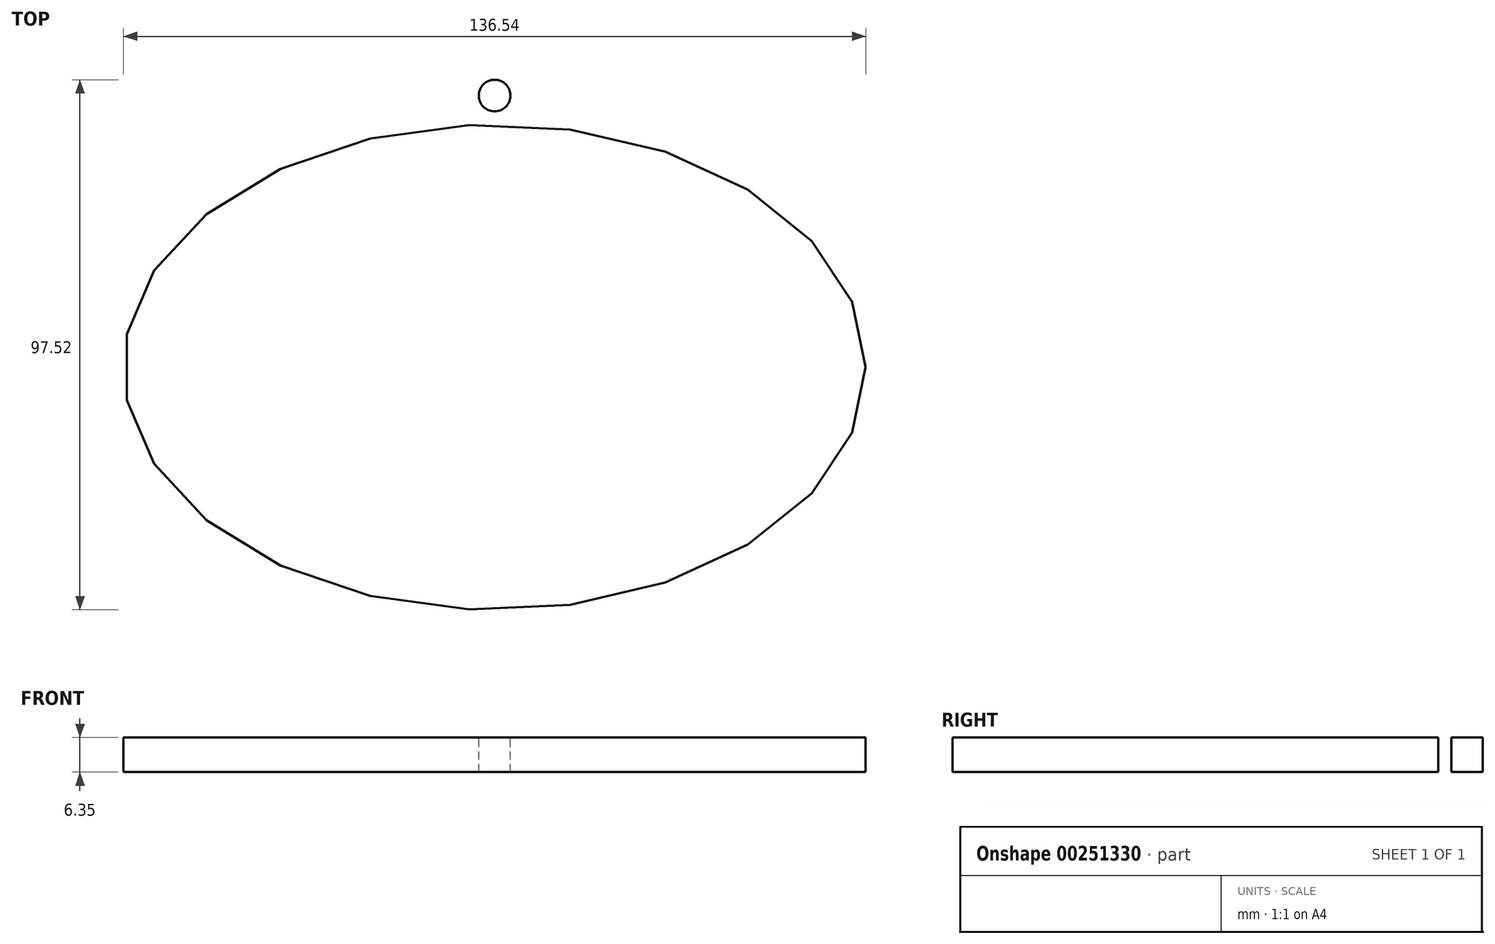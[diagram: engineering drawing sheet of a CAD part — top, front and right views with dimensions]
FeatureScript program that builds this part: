
annotation { "Feature Type Name" : "Feature", "Feature Type Description" : "" }
export const myFeature = defineFeature(function(context is Context, id is Id, definition is map)
    precondition{}
    {
        {
            var Q0;
            Q0=qCreatedBy(makeId("Top.planeOp"),FACE);
            var sketch = newSketch(context, id + "F0", { "sketchPlane" : qUnion([Q0])});
            skEllipse(sketch, "E0", {"center": v(-42.45, 33.5) * mm, "majorRadius": 68.27 * mm, "minorRadius": 44.64 * mm, "majorAxis": v(1, 0)});
            skFitSpline(sketch, "E1.0", {"points": [v(35.9, 30.52) * mm, v(36.01, 33.5) * mm, v(35.9, 36.5) * mm, v(35.45, 40.43) * mm, v(34.34, 45.26) * mm, v(32.2, 50.82) * mm, v(29.32, 56.08) * mm, v(25.75, 61) * mm, v(21.56, 65.59) * mm, v(17.58, 69.1) * mm, v(14.13, 71.72) * mm, v(11.4, 73.6) * mm, v(8.56, 75.36) * mm, v(4.65, 77.56) * mm, v(-0.46, 80.03) * mm, v(-6.91, 82.55) * mm, v(-13.63, 84.63) * mm, v(-20.58, 86.26) * mm, v(-27.73, 87.43) * mm, v(-33.81, 88.03) * mm, v(-38.73, 88.27) * mm, v(-42.45, 88.33) * mm, v(-46.17, 88.27) * mm, v(-51.1, 88.03) * mm, v(-57.18, 87.43) * mm, v(-64.32, 86.26) * mm, v(-71.27, 84.63) * mm, v(-78, 82.55) * mm, v(-84.44, 80.03) * mm, v(-89.55, 77.56) * mm, v(-93.46, 75.36) * mm, v(-96.3, 73.6) * mm, v(-99.03, 71.72) * mm, v(-102.48, 69.1) * mm, v(-106.46, 65.59) * mm, v(-110.65, 61) * mm, v(-114.22, 56.08) * mm, v(-117.1, 50.82) * mm, v(-119.25, 45.26) * mm, v(-120.35, 40.43) * mm, v(-120.8, 36.5) * mm, v(-120.92, 33.5) * mm, v(-120.8, 30.52) * mm, v(-120.35, 26.57) * mm, v(-119.25, 21.74) * mm, v(-117.1, 16.19) * mm, v(-114.22, 10.93) * mm, v(-110.65, 6) * mm, v(-106.46, 1.42) * mm, v(-102.48, -2.1) * mm, v(-99.03, -4.71) * mm, v(-96.3, -6.59) * mm, v(-93.46, -8.35) * mm, v(-89.55, -10.55) * mm, v(-84.44, -13.03) * mm, v(-78, -15.55) * mm, v(-71.27, -17.62) * mm, v(-64.32, -19.25) * mm, v(-57.18, -20.43) * mm, v(-51.1, -21.02) * mm, v(-46.17, -21.26) * mm, v(-42.45, -21.32) * mm, v(-38.73, -21.26) * mm, v(-33.81, -21.02) * mm, v(-27.73, -20.43) * mm, v(-20.58, -19.25) * mm, v(-13.63, -17.62) * mm, v(-6.91, -15.55) * mm, v(-0.46, -13.03) * mm, v(4.65, -10.55) * mm, v(8.56, -8.35) * mm, v(11.4, -6.59) * mm, v(14.13, -4.71) * mm, v(17.58, -2.1) * mm, v(21.56, 1.42) * mm, v(25.75, 6) * mm, v(29.32, 10.93) * mm, v(32.2, 16.19) * mm, v(34.34, 21.74) * mm, v(35.45, 26.57) * mm, v(35.9, 30.52) * mm, v(36.01, 33.5) * mm, v(35.9, 36.5) * mm, v(35.9, 30.52) * mm]});
            skCircle(sketch, "E2", {"center": v(-42.45, 83.47) * mm, "radius": 2.9 * mm});
            skLineSegment(sketch, "E3", {"start": v(-79.12, -4.15) * mm, "end": v(-58.15, -4.15) * mm});
            skLineSegment(sketch, "E4", {"start": v(-58.15, -4.15) * mm, "end": v(-58.15, 4.8) * mm});
            skLineSegment(sketch, "E5", {"start": v(-58.15, 4.8) * mm, "end": v(-37.17, 4.8) * mm});
            skLineSegment(sketch, "E6", {"start": v(-37.17, 4.8) * mm, "end": v(-37.17, 13.76) * mm});
            skLineSegment(sketch, "E7", {"start": v(-37.17, 13.76) * mm, "end": v(-16.2, 13.76) * mm});
            skLineSegment(sketch, "E8", {"start": v(-16.2, 13.76) * mm, "end": v(-16.2, 22.72) * mm});
            skLineSegment(sketch, "E9", {"start": v(-16.2, 22.72) * mm, "end": v(4.78, 22.72) * mm});
            skLineSegment(sketch, "E10", {"start": v(4.78, 22.72) * mm, "end": v(4.78, 31.68) * mm});
            skLineSegment(sketch, "E11", {"start": v(4.78, 31.68) * mm, "end": v(25.76, 31.68) * mm});
            skLineSegment(sketch, "E12", {"start": v(-47.5, -11.02) * mm, "end": v(23.14, 21.12) * mm});
            skLineSegment(sketch, "E13.top", {"start": v(5.55, 31.68) * mm, "end": v(6.88, 31.68) * mm});
            skLineSegment(sketch, "E14", {"start": v(-72.89, 73.46) * mm, "end": v(-109.22, 42.8) * mm});
            skLineSegment(sketch, "E15", {"start": v(-64.18, 75.82) * mm, "end": v(-110.54, 36.7) * mm});
            skLineSegment(sketch, "E16", {"start": v(-79.16, 63.19) * mm, "end": v(-10.33, 72.9) * mm});
            skLineSegment(sketch, "E17", {"start": v(-83.94, 59.15) * mm, "end": v(-4.3, 70.52) * mm});
            skSolve(sketch);
        }
        {
            var Q0;
            Q0 = qSketchRegion(id + "F0", true);
            var Q1;
            {var subQ4=sQuery(id+"F0.wireOp",EDGE,"E14");Q1=makeQuery(id+"F0.imprint","IMPRINT",FACE,{"disambiguationData":[TD([[makeQuery(id+"F0.imprint","IMPRINT",EDGE,{"derivedFrom":subQ4}),1.0]])]});}
            var Q2;
            {var subQ0=sQuery(id+"F0.wireOp",EDGE,"E16");Q2=makeQuery(id+"F0.imprint","IMPRINT",FACE,{"disambiguationData":[TD([[makeQuery(id+"F0.imprint","IMPRINT",EDGE,{"derivedFrom":subQ0}),-1.0]])]});}
            var Q3;
            {var subQ0=sQuery(id+"F0.wireOp",EDGE,"E3");Q3=makeQuery(id+"F0.imprint","IMPRINT",FACE,{"disambiguationData":[TD([[makeQuery(id+"F0.imprint","IMPRINT",EDGE,{"derivedFrom":subQ0}),-1.0]])]});}
            extrude(context, id + "F1", {"entities" : qUnion([Q0, Q1, Q2, Q3]), "oppositeDirection" : true, "depth" : 6.35 * mm});
        }
    });
